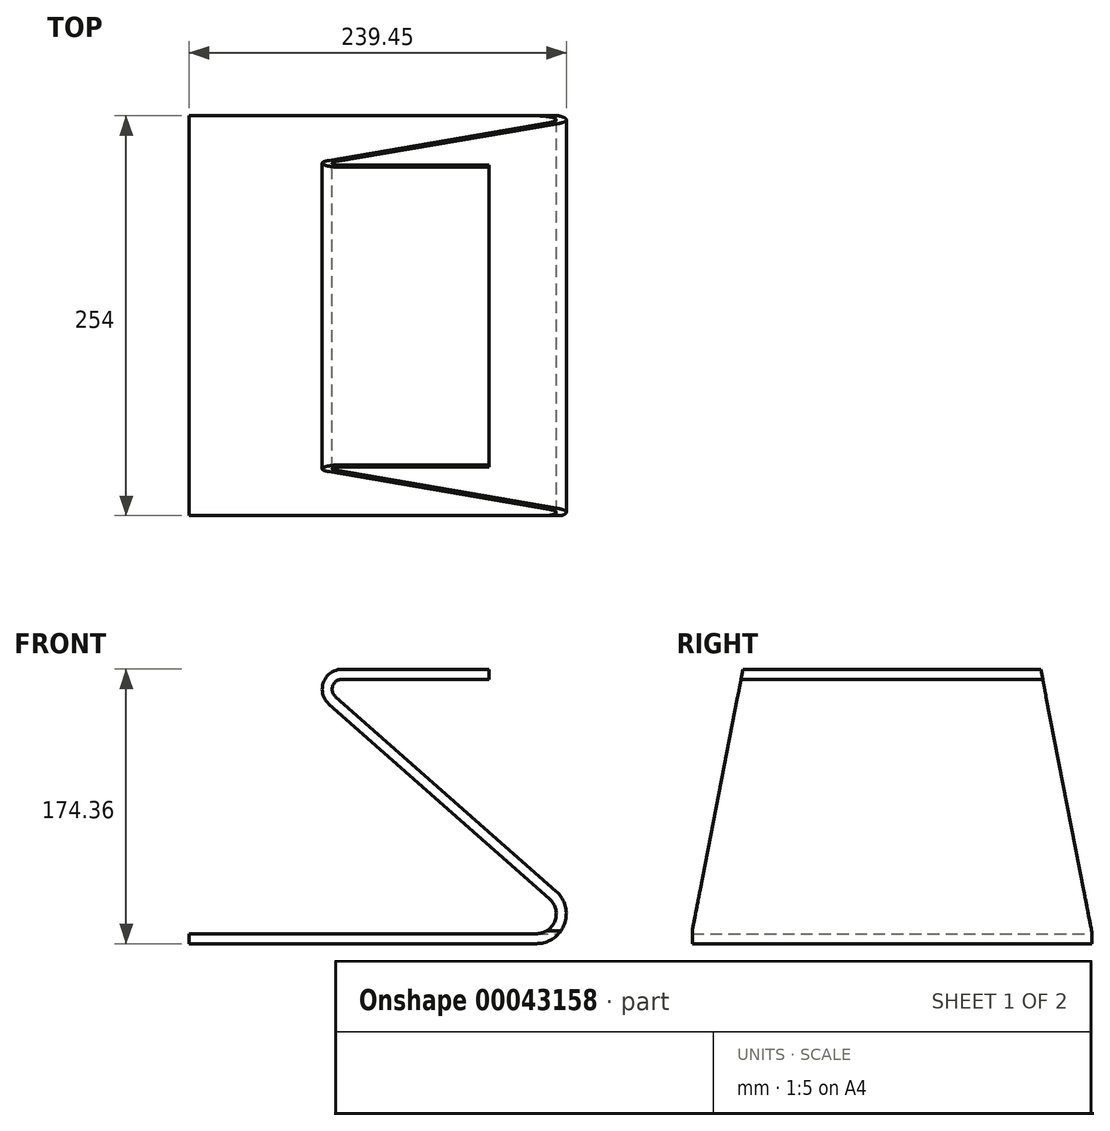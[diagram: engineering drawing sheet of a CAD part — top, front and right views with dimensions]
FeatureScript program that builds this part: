
annotation { "Feature Type Name" : "Feature", "Feature Type Description" : "" }
export const myFeature = defineFeature(function(context is Context, id is Id, definition is map)
    precondition{}
    {
        {
            var Q0;
            Q0=qCreatedBy(makeId("Front.planeOp"),FACE);
            var sketch = newSketch(context, id + "F0", { "sketchPlane" : qUnion([Q0])});
            skLineSegment(sketch, "E0", {"start": v(-254, 0) * mm, "end": v(-33.6, 0) * mm});
            skLineSegment(sketch, "E1", {"start": v(-25.2, 22.23) * mm, "end": v(-165.3, 145.78) * mm});
            skLineSegment(sketch, "E2", {"start": v(-156.9, 168) * mm, "end": v(-63.5, 168) * mm});
            skLineSegment(sketch, "E3", {"start": v(-127, 168) * mm, "end": v(-127, 0) * mm, "construction": true});
            skPoint(sketch, "E4.visualSharp", {"position": v(0, 0) * mm});
            skArc(sketch, "E4.filletArc", {"start": v(-33.6, 0) * mm, "mid": v(-21.72, 8.2) * mm, "end": v(-25.2, 22.23) * mm});
            skPoint(sketch, "E5.visualSharp", {"position": v(-190.5, 168) * mm});
            skArc(sketch, "E5.filletArc", {"start": v(-156.9, 168) * mm, "mid": v(-168.78, 159.8) * mm, "end": v(-165.3, 145.78) * mm});
            skLineSegment(sketch, "E6.0", {"start": v(-156.9, 161.66) * mm, "end": v(-63.5, 161.66) * mm});
            skLineSegment(sketch, "E6.1", {"start": v(-254, -6.35) * mm, "end": v(-33.6, -6.35) * mm});
            skArc(sketch, "E6.2", {"start": v(-33.6, -6.35) * mm, "mid": v(-15.78, 5.96) * mm, "end": v(-21, 26.99) * mm});
            skLineSegment(sketch, "E6.3", {"start": v(-21, 26.99) * mm, "end": v(-161.1, 150.54) * mm});
            skArc(sketch, "E6.4", {"start": v(-156.9, 161.66) * mm, "mid": v(-162.84, 157.55) * mm, "end": v(-161.1, 150.54) * mm});
            skLineSegment(sketch, "E7", {"start": v(-63.5, 168) * mm, "end": v(-63.5, 161.66) * mm});
            skLineSegment(sketch, "E8", {"start": v(-254, 0) * mm, "end": v(-254, -6.35) * mm});
            skSolve(sketch);
        }
        {
            var Q0;
            Q0 = qSketchRegion(id + "F0", true);
            extrude(context, id + "F1", {"entities" : qUnion([Q0]), "depth" : 254 * mm});
        }
        {
            var Q0;
            Q0=qCreatedBy(makeId("Right.planeOp"),FACE);
            var sketch = newSketch(context, id + "F2", { "sketchPlane" : qUnion([Q0])});
            skLineSegment(sketch, "E9", {"start": v(0, 0) * mm, "end": v(-33.32, 171.58) * mm});
            skLineSegment(sketch, "E10", {"start": v(-33.32, 171.58) * mm, "end": v(15.1, 171.58) * mm});
            skLineSegment(sketch, "E11", {"start": v(15.1, 171.58) * mm, "end": v(15.1, 0) * mm});
            skLineSegment(sketch, "E12", {"start": v(15.1, 0) * mm, "end": v(0, 0) * mm});
            skLineSegment(sketch, "E13", {"start": v(0, 0) * mm, "end": v(-254.37, 0) * mm, "construction": true});
            skLineSegment(sketch, "E14", {"start": v(-254.37, 0) * mm, "end": v(-127.19, 0) * mm, "construction": true});
            skLineSegment(sketch, "E15", {"start": v(-127.19, 0) * mm, "end": v(-127.19, 167.8) * mm, "construction": true});
            skLineSegment(sketch, "E16.MirrorCS", {"start": v(-221.05, 171.58) * mm, "end": v(-269.47, 171.58) * mm});
            skLineSegment(sketch, "E17.MirrorCS", {"start": v(-269.47, 171.58) * mm, "end": v(-269.47, 0) * mm});
            skLineSegment(sketch, "E18.MirrorCS", {"start": v(-254.37, 0) * mm, "end": v(-221.05, 171.58) * mm});
            skLineSegment(sketch, "E19.MirrorCS", {"start": v(-269.47, 0) * mm, "end": v(-254.37, 0) * mm});
            skSolve(sketch);
        }
        {
            var Q0;
            Q0 = qSketchRegion(id + "F2", true);
            extrude(context, id + "F3", {"entities" : qUnion([Q0]), "operationType" : NewBodyOperationType.REMOVE, "endBound" : BoundingType.THROUGH_ALL, "oppositeDirection" : true, "depth" : 25.4 * mm});
        }
    });
